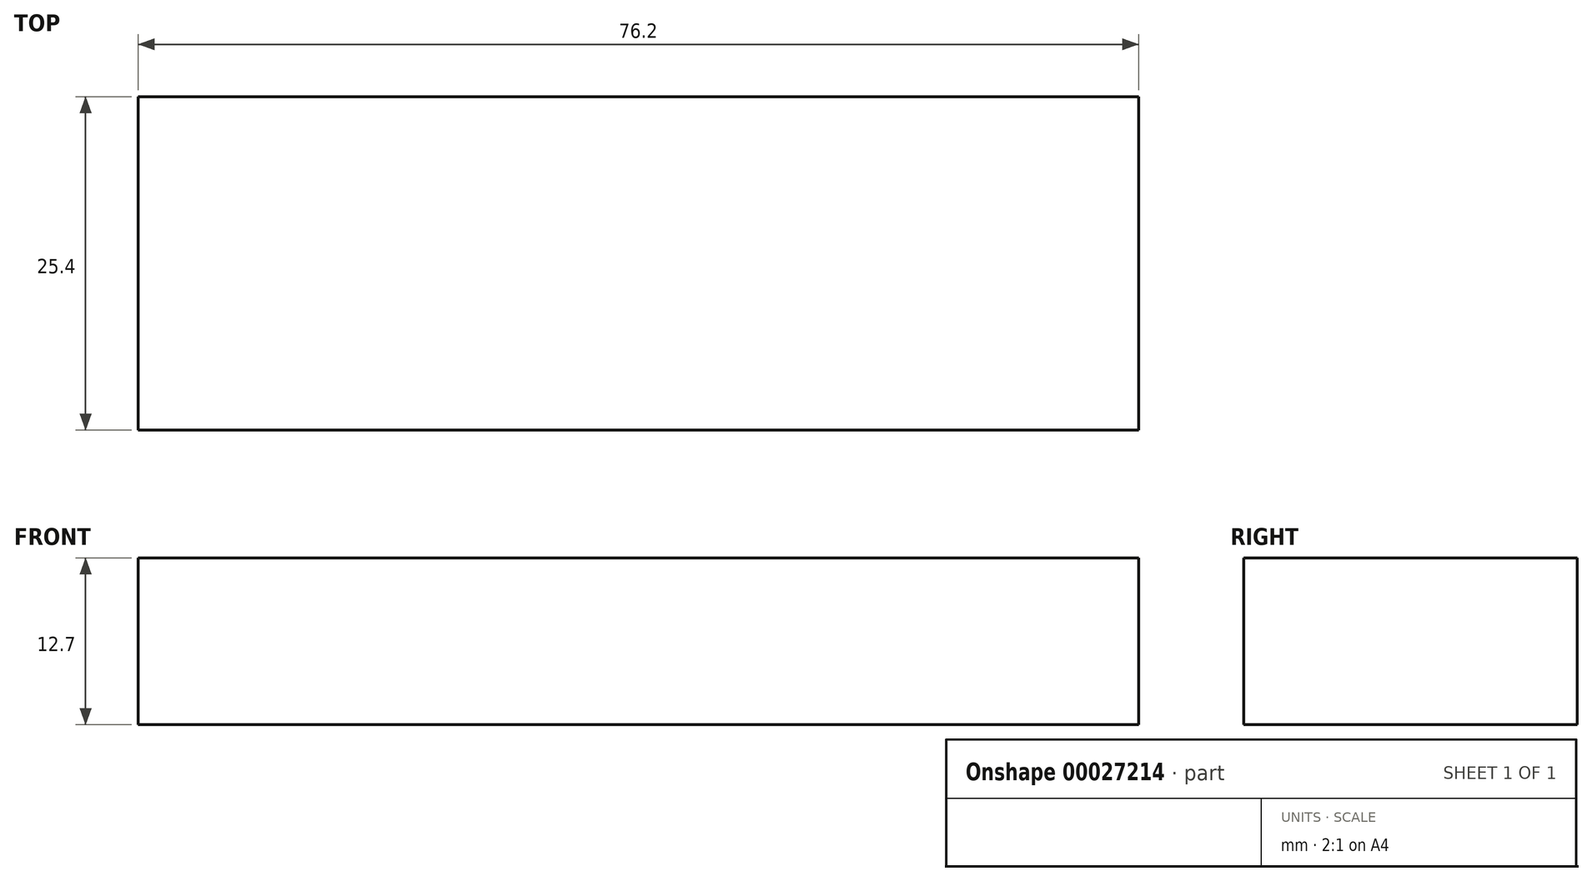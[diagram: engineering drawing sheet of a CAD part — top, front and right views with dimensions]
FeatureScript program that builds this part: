
annotation { "Feature Type Name" : "Feature", "Feature Type Description" : "" }
export const myFeature = defineFeature(function(context is Context, id is Id, definition is map)
    precondition{}
    {
        {
            var Q0;
            Q0=qCreatedBy(makeId("Front.planeOp"),FACE);
            var sketch = newSketch(context, id + "F0", { "sketchPlane" : qUnion([Q0])});
            skLineSegment(sketch, "E0.bottom", {"start": v(0, 0) * mm, "end": v(76.2, 0) * mm});
            skLineSegment(sketch, "E0.top", {"start": v(0, 12.7) * mm, "end": v(76.2, 12.7) * mm});
            skLineSegment(sketch, "E0.left", {"start": v(0, 0) * mm, "end": v(0, 12.7) * mm});
            skLineSegment(sketch, "E0.right", {"start": v(76.2, 0) * mm, "end": v(76.2, 12.7) * mm});
            skSolve(sketch);
        }
        {
            var Q0;
            Q0=makeQuery(id+"F0.imprint","IMPRINT",FACE,{"disambiguationData":[TD([[makeQuery(id+"F0.imprint","IMPRINT",EDGE,{"derivedFrom":sQuery(id+"F0.wireOp",EDGE,"E0.bottom")}),1.0]])]});
            extrude(context, id + "F1", {"entities" : qUnion([Q0]), "depth" : 25.4 * mm});
        }
    });
